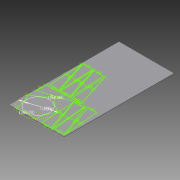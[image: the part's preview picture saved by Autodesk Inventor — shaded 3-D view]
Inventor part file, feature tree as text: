
AUTODESK INVENTOR PART (.ipt)
format: ipt  version: 2015 (Build 190159000, 159)  size: 167,936 bytes
history: native  units: in
note: dims shown in document units (in); Inventor stores cm internally (conversion verified against a paired STEP export)
features: sketch x3, extrude x1
ambient origin geometry x8: Origin, YZ Plane, XZ Plane, XY Plane, X Axis, Y Axis, Z Axis, Center Point
bodies: Solid1 (feature_tree)
feature tree (4):
  extrude  "Extrusion1"  Depth=24.0in
  sketch  "Sketch2"  dims[d2=0.125in d3=0.0in]
  sketch  "Sketch3"  dims[d5=1.9685in d7=1.9685in d8=5.0in d9=7.0in d10=360.0deg d11=360.0deg d13=1.9685in d15=1.9685in d17=1.9685in d19=1.9685in d21=1.9685in d23=1.9685in d25=1.9685in d27=1.9685in d29=1.9685in d31=1.9685in d33=1.9685in d35=1.9685in d37=1.9685in d39=1.9685in]
  sketch  "Sketch1"  dims[d0=12.0in d1=24.0in]
